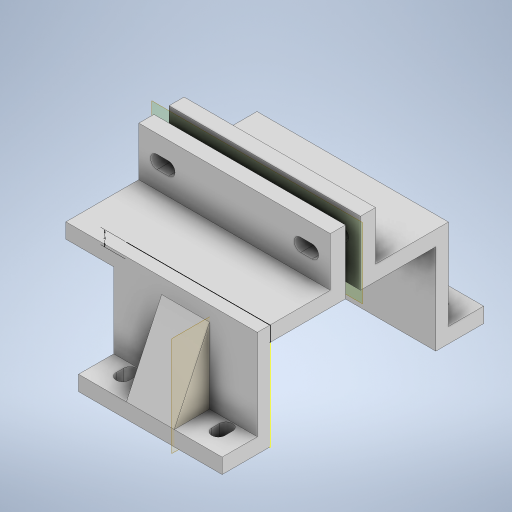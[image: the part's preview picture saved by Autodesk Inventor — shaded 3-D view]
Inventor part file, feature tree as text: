
AUTODESK INVENTOR PART (.ipt)
format: ipt  version: 2023.1 (Build 271208000, 208)  size: 414,720 bytes
history: native  units: mm
features: extrude x8, sketch x7, projected_geometry x5, other x3, plane x2, mirror x1
ambient origin geometry x8: Origin, YZ Plane, XZ Plane, XY Plane, X Axis, Y Axis, Z Axis, Center Point
bodies: Body1 (feature_tree), Body2 (feature_tree)
feature tree (26):
  other  "Left"
  extrude  "Extrusion1"  Depth=12.7mm
  extrude  "Extrusion2"  Depth=12.7mm
  plane  "Work Plane1"
  extrude  "Extrusion3"  Depth=24.0mm
  sketch  "Sketch4"  dims[d9=3.35mm d10=10.0mm d11=0.0mm]
  extrude  "Extrusion4"  Depth=10.0mm TaperAngle=0.0deg
  extrude  "Extrusion5"  Depth=25.4mm
  extrude  "Extrusion6"  Depth=3.5mm
  extrude  "Extrusion7"  Depth=3.5mm
  extrude  "Extrusion8"  [1 undecoded]
  plane  "Work Plane2"
  mirror  "Mirror1"
  sketch  "Sketch1"  dims[d0=38.1mm d1=12.7mm]
  sketch  "Sketch2"  dims[d2=12.7mm d3=12.7mm]
  projected_geometry  "Projected Loop1"
  sketch  "Sketch3"  dims[d6=4.0mm d7=0.0mm d8=24.0mm]
  projected_geometry  "Projected Loop2"
  projected_geometry  "Projected Loop3"
  sketch  "Sketch5"  dims[d12=25.4mm d13=2.0mm]
  projected_geometry  "Projected Loop4"
  sketch  "Sketch6"  dims[d14=3.5mm d15=3.5mm]
  sketch  "Sketch7"  dims[d16=3.5mm d17=3.5mm d18=-12.7mm d19=12.7mm d20=0.0mm d21=4.0mm d22=12.7mm d23=0.0mm d24=20.0mm d25=0.0mm d26=12.7mm d27=0.0mm d28=4.0mm d29=13.0mm d30=0.0mm d31=6.35mm d32=6.35mm d33=3.0mm d34=2.0mm d35=3.0mm d36=2.0mm d37=3.5mm d38=3.5mm d39=13.0mm d40=0.0mm d41=2.0mm]
  projected_geometry  "Projected Loop5"
  other  "Pattern of Left:1"
  other  "Right"
note: 1 required parameter value undecoded (feature->parameter linkage not recoverable at this tier; creation-order binding heuristic only, values carry confidence <= 0.55)
